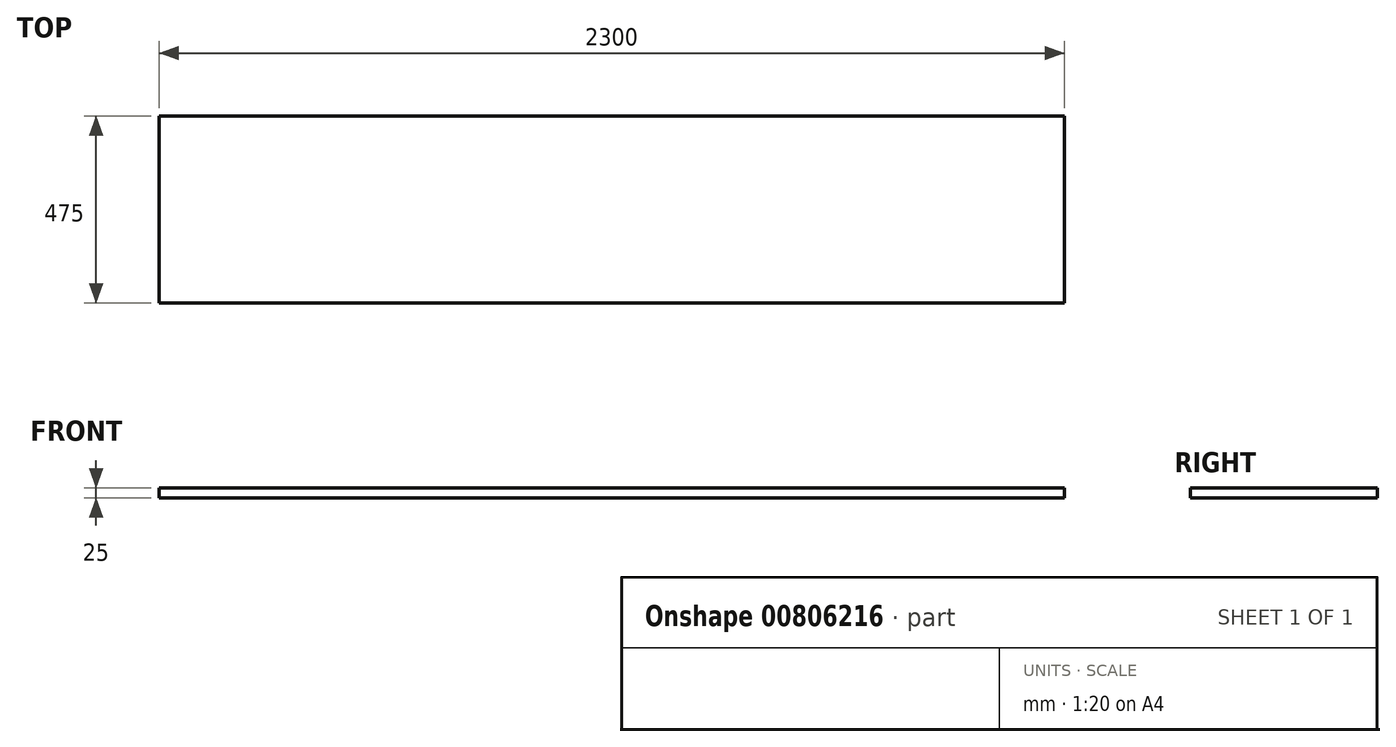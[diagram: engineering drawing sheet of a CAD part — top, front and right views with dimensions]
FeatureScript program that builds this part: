
annotation { "Feature Type Name" : "Feature", "Feature Type Description" : "" }
export const myFeature = defineFeature(function(context is Context, id is Id, definition is map)
    precondition{}
    {
        {
            var Q0;
            Q0=qCreatedBy(makeId("Top.planeOp"),FACE);
            var sketch = newSketch(context, id + "F0", { "sketchPlane" : qUnion([Q0])});
            skLineSegment(sketch, "E0.bottom", {"start": v(1150, -237.5) * mm, "end": v(-1150, -237.5) * mm});
            skLineSegment(sketch, "E0.top", {"start": v(1150, 237.5) * mm, "end": v(-1150, 237.5) * mm});
            skLineSegment(sketch, "E0.left", {"start": v(1150, -237.5) * mm, "end": v(1150, 237.5) * mm});
            skLineSegment(sketch, "E0.right", {"start": v(-1150, -237.5) * mm, "end": v(-1150, 237.5) * mm});
            skPoint(sketch, "E0.middle", {"position": v(0, 0) * mm});
            skSolve(sketch);
        }
        {
            var Q0;
            Q0=qSketchRegion(id+"F0",true);
            extrude(context, id + "F1", {"entities" : qUnion([Q0]), "depth" : 25 * mm, "offsetDistance" : 25 * mm});
        }
    });
